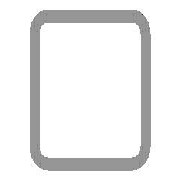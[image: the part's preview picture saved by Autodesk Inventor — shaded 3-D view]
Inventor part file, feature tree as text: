
AUTODESK INVENTOR PART (.ipt)
format: ipt  version: 2023.1 (Build 271208000, 208)  size: 129,536 bytes
history: native  units: mm (DEFAULTED — no unit token found)
features: other x4, sketch x3, plane x1
ambient origin geometry x8: Origin, YZ Plane, XZ Plane, XY Plane, X Axis, Y Axis, Z Axis, Center Point
bodies: Solid1 (feature_tree), Body (feature_tree)
feature tree (8):
  parser-record x1  (decoder bookkeeping rows leaked as tree rows — omitted from the tree; the rows remain in map.json)
  other  "Driven Length"
  other  "Start Plane"
  other  "End Plane"
  sketch  "Sketch"  dims[d10=50.8mm d11=50.8mm d12=3.175mm d13=-0.0mm d14=482.6mm d15=25.4mm d16=25.4mm d17=6.35mm d18=90.0deg d19=482.6mm]
  sketch  "Sketch3"  dims[d3=482.6mm]
  plane  "Work Plane3"
  sketch  "Sketch4"  dims[d4=0.0mm]
